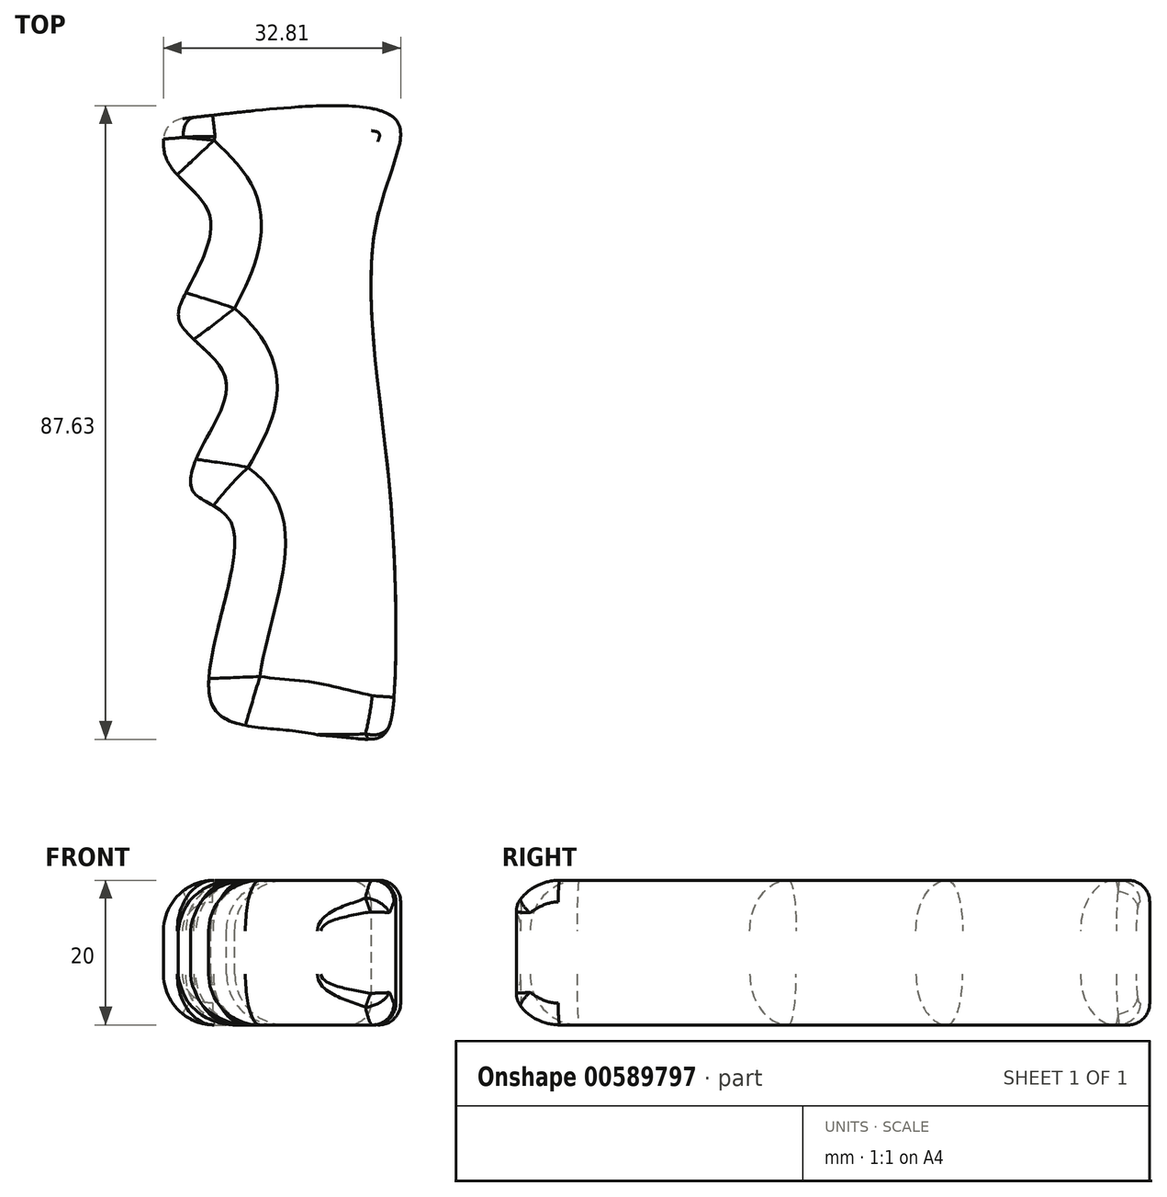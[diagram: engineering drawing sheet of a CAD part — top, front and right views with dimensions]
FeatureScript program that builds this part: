
annotation { "Feature Type Name" : "Feature", "Feature Type Description" : "" }
export const myFeature = defineFeature(function(context is Context, id is Id, definition is map)
    precondition{}
    {
        {
            var Q0;
            Q0=qCreatedBy(makeId("Top.planeOp"),FACE);
            var sketch = newSketch(context, id + "F0", { "sketchPlane" : qUnion([Q0])});
            skLineSegment(sketch, "E0", {"start": v(25.07, -4.34) * mm, "end": v(25.07, 80.66) * mm});
            skLineSegment(sketch, "E1", {"start": v(4.07, 80.66) * mm, "end": v(35.78, 80.66) * mm});
            skFitSpline(sketch, "E2", {"points": [v(4.07, 80.66) * mm, v(4.07, 75.08) * mm, v(9.95, 67.46) * mm, v(6.61, 56.77) * mm, v(6.08, 52.23) * mm, v(12.09, 45.15) * mm, v(8.75, 35.27) * mm, v(7.81, 29.12) * mm, v(13.16, 24.45) * mm, v(10.22, 0) * mm, v(25.07, -4.34) * mm], "startDerivative": vector(-15.15, -45.53) * mm, "endDerivative": vector(142.8, -34.11) * mm});
            skFitSpline(sketch, "E3", {"points": [v(25.07, -4.34) * mm, v(33.96, -4.34) * mm, v(35.55, 2.8) * mm, v(34.71, 31.1) * mm, v(33.11, 67.17) * mm, v(35.78, 80.66) * mm, v(4.07, 80.66) * mm], "startDerivative": vector(134.77, -8.42) * mm, "endDerivative": vector(-201.4, -22.72) * mm});
            skSolve(sketch);
        }
        {
            var Q0;
            Q0 = qSketchRegion(id + "F0", true);
            extrude(context, id + "F1", {"entities" : qUnion([Q0]), "depth" : 20 * mm, "offsetDistance" : 25 * mm});
        }
        {
            var Q0;
            Q0=makeQuery(id+"F1.opExtrude","CAP_EDGE",EDGE,{"disambiguationData":[OSD([sQuery(id+"F0.wireOp",EDGE,"E2")])],"isStart":false});
            var Q1;
            Q1=makeQuery(id+"F1.opExtrude","CAP_EDGE",EDGE,{"disambiguationData":[OSD([sQuery(id+"F0.wireOp",EDGE,"E2")])],"isStart":true});
            fillet(context, id + "F2", {"entities" : qUnion([Q0, Q1]), "radius" : 7 * mm, "tangentPropagation" : true, "allowEdgeOverflow" : false});
        }
        {
            var Q0;
            Q0=makeQuery(id+"F1.opExtrude","CAP_EDGE",EDGE,{"disambiguationData":[OSD([sQuery(id+"F0.wireOp",EDGE,"E3")])],"isStart":false});
            fillet(context, id + "F3", {"entities" : qUnion([Q0]), "radius" : 3 * mm, "tangentPropagation" : true, "allowEdgeOverflow" : false});
        }
    });
